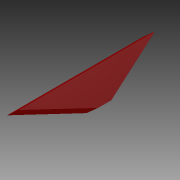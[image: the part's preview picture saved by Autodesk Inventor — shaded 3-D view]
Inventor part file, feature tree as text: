
AUTODESK INVENTOR PART (.ipt)
format: ipt  version: 2014 (Build 180170000, 170)  size: 788,992 bytes
history: native  units: in
note: dims shown in document units (in); Inventor stores cm internally (conversion verified against a paired STEP export)
features: sketch x23, extrude x16, plane x9, projected_geometry x6, loft x4, other x3, mirror x1, emboss x1
ambient origin geometry x8: Origin, YZ Plane, XZ Plane, XY Plane, X Axis, Y Axis, Z Axis, Center Point
bodies: Solid1 (feature_tree)
feature tree (63):
  sketch  "Sketch1"  dims[d0=0.7559in d1=0.7559in]
  plane  "Work Plane1"
  loft  "Loft1"
  extrude  "Extrusion1"  Depth=0.2in
  plane  "Work Plane4"
  loft  "Loft2"
  plane  "Work Plane5"
  loft  "Loft3"
  loft  "Loft4"
  extrude  "Extrusion2"  TaperAngle=0.0deg  [1 undecoded]
  plane  "Work Plane6"
  extrude  "Extrusion3"  Depth=1.0in
  extrude  "Extrusion4"  Depth=1.0651in
  extrude  "Extrusion5"  Depth=0.962in
  plane  "Work Plane7"
  extrude  "Extrusion6"  Depth=0.075in
  plane  "Work Plane8"
  other  "Work Axis1"
  plane  "Work Plane9"
  extrude  "Extrusion7"  Depth=0.06in
  mirror  "Mirror3"
  extrude  "Extrusion8"  Depth=0.05in
  plane  "Work Plane10"
  extrude  "Extrusion9"  Depth=0.0625in
  plane  "Work Plane11"
  extrude  "Extrusion10"  Depth=0.075in
  extrude  "Extrusion11"  TaperAngle=0.0deg  [1 undecoded]
  extrude  "Extrusion12"  Depth=0.2in
  extrude  "Extrusion13"  TaperAngle=0.0deg  [1 undecoded]
  emboss  "Emboss1"
  extrude  "Extrusion15"  Depth=0.01in
  extrude  "Extrusion16"  Depth=0.0344in
  extrude  "Extrusion17"  TaperAngle=60.0deg  [1 undecoded]
  sketch  "Sketch2"  dims[d2=0.9963in d3=0.2in]
  sketch  "Sketch3"  dims[d4=0.5in d6=0.08in]
  sketch  "Sketch4"  dims[d7=0.55in d8=150.0deg]
  other  "Edges1"
  sketch  "Sketch5"  dims[d9=150.0deg d14=0.33in]
  projected_geometry  "Projected Loop1"
  other  "Edges2"
  sketch  "Sketch6"  dims[d15=0.66in d18=0.0in d19=90.0deg]
  sketch  "Sketch7"  dims[d20=0.0in d21=90.0deg d22=1.0in]
  sketch  "Sketch8"  dims[d26=1.0651in d28=1.0651in]
  sketch  "Sketch9"  dims[d29=0.0in d30=0.962in]
  sketch  "Sketch10"  dims[d31=0.962in d32=0.075in]
  sketch  "Sketch11"  dims[d33=0.15in d34=0.06in]
  sketch  "Sketch12"  dims[d35=0.1in d36=0.05in]
  sketch  "Sketch13"  dims[d37=0.45in d38=0.0in d39=0.0625in]
  projected_geometry  "Projected Loop2"
  projected_geometry  "Projected Loop3"
  sketch  "Sketch14"  dims[d40=0.01in d41=0.075in]
  projected_geometry  "Projected Loop4"
  sketch  "Sketch15"  dims[d42=0.01in d43=0.0in d44=90.0deg]
  sketch  "Sketch16"  dims[d45=0.0in d46=90.0deg d47=0.2in]
  sketch  "Sketch17"  dims[d48=0.07in d49=0.0in d50=90.0deg]
  sketch  "Sketch18"  dims[d51=0.0in d52=90.0deg d53=0.01in]
  sketch  "Sketch19"  dims[d54=0.01in d55=0.0344in]
  sketch  "Sketch20"  dims[d56=150.0deg d57=60.0deg]
  sketch  "Sketch22"  dims[d58=150.0deg]
  projected_geometry  "Projected Loop5"
  sketch  "Sketch23"  dims[d59=0.7in]
  projected_geometry  "Projected Loop6"
  sketch  "Sketch24"  dims[d60=0.05in d61=0.05in d62=0.05in d63=0.05in d64=0.05in d65=0.01in d66=0.0in d67=90.0deg d68=0.0in d69=90.0deg d70=0.1in d71=0.4in d72=0.15in d73=0.05in d74=0.0in d75=0.02in d77=0.15in d78=0.02in d79=0.1in d80=0.1in d81=0.1in d82=0.02in d83=0.15in d84=0.05in d85=0.0in d86=0.045in d87=0.0in d88=0.025in d89=0.0in d90=0.02in d91=0.02in d92=0.005in d93=0.0in d94=90.0deg d95=0.4466in d96=1.0in d97=0.0in d98=1.0in d99=0.0in d100=0.6528in d101=0.0in d102=0.0in d103=1.0in d104=0.0in d106=90.0deg d107=1.0in d108=0.0in d109=1.65in d110=0.1in d111=0.075in d112=0.0in d113=0.1in d114=0.075in d115=0.0in d116=0.05in d117=0.0in d121=0.05in d122=0.0in d123=0.1in d124=0.0in d125=0.05in d126=0.0in]
note: 4 required parameter values undecoded (feature->parameter linkage not recoverable at this tier; creation-order binding heuristic only, values carry confidence <= 0.55)
